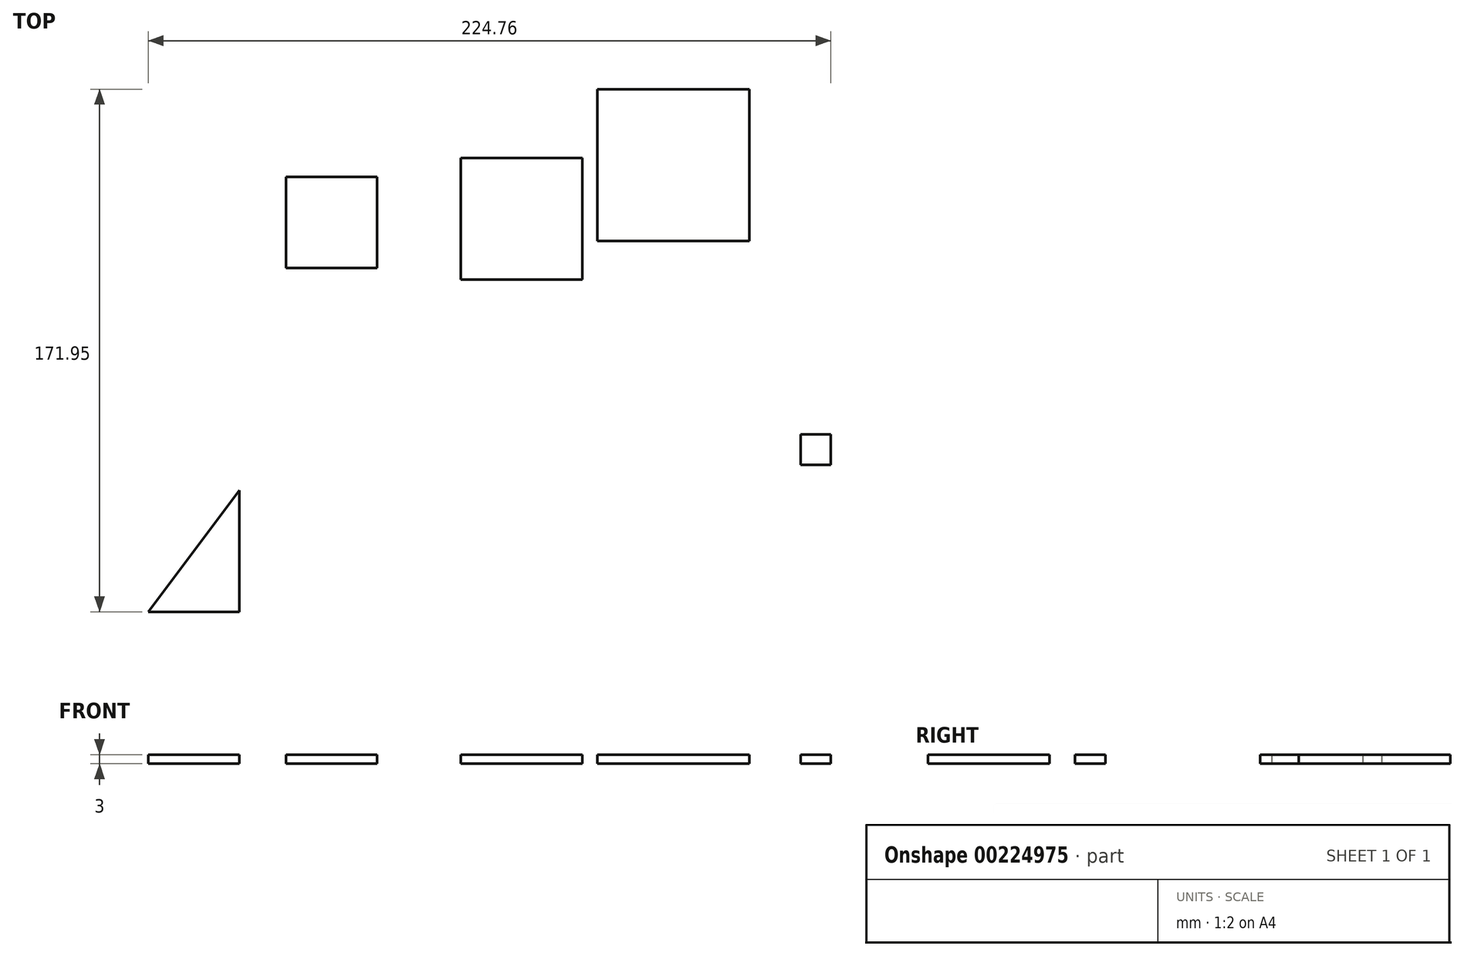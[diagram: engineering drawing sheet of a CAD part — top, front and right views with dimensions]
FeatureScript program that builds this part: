
annotation { "Feature Type Name" : "Feature", "Feature Type Description" : "" }
export const myFeature = defineFeature(function(context is Context, id is Id, definition is map)
    precondition{}
    {
        {
            var Q0;
            Q0=qCreatedBy(makeId("Top.planeOp"),FACE);
            var sketch = newSketch(context, id + "F0", { "sketchPlane" : qUnion([Q0])});
            skLineSegment(sketch, "E0", {"start": v(-120.88, -43.88) * mm, "end": v(-90.88, -43.88) * mm});
            skLineSegment(sketch, "E1", {"start": v(-90.88, -43.88) * mm, "end": v(-90.88, -3.88) * mm});
            skLineSegment(sketch, "E2", {"start": v(-90.88, -3.88) * mm, "end": v(-120.88, -43.88) * mm});
            skLineSegment(sketch, "E3.0.1.1", {"start": v(-121.07, 6.12) * mm, "end": v(-91.07, 6.12) * mm});
            skLineSegment(sketch, "E3.direction1", {"start": v(-120.88, -43.88) * mm, "end": v(-80.9, -42.52) * mm, "construction": true});
            skLineSegment(sketch, "E3.direction2", {"start": v(-120.88, -43.88) * mm, "end": v(-121.07, 6.12) * mm, "construction": true});
            skLineSegment(sketch, "E4.bottom", {"start": v(-75.5, 99.2) * mm, "end": v(-45.5, 99.2) * mm});
            skLineSegment(sketch, "E4.top", {"start": v(-75.5, 69.2) * mm, "end": v(-45.5, 69.2) * mm});
            skLineSegment(sketch, "E4.left", {"start": v(-75.5, 99.2) * mm, "end": v(-75.5, 69.2) * mm});
            skLineSegment(sketch, "E4.right", {"start": v(-45.5, 99.2) * mm, "end": v(-45.5, 69.2) * mm});
            skLineSegment(sketch, "E5.bottom", {"start": v(-17.95, 105.45) * mm, "end": v(22.05, 105.45) * mm});
            skLineSegment(sketch, "E5.top", {"start": v(-17.95, 65.45) * mm, "end": v(22.05, 65.45) * mm});
            skLineSegment(sketch, "E5.left", {"start": v(-17.95, 105.45) * mm, "end": v(-17.95, 65.45) * mm});
            skLineSegment(sketch, "E5.right", {"start": v(22.05, 105.45) * mm, "end": v(22.05, 65.45) * mm});
            skLineSegment(sketch, "E6.bottom", {"start": v(26.98, 128.07) * mm, "end": v(76.98, 128.07) * mm});
            skLineSegment(sketch, "E6.top", {"start": v(26.98, 78.07) * mm, "end": v(76.98, 78.07) * mm});
            skLineSegment(sketch, "E6.left", {"start": v(26.98, 128.07) * mm, "end": v(26.98, 78.07) * mm});
            skLineSegment(sketch, "E6.right", {"start": v(76.98, 128.07) * mm, "end": v(76.98, 78.07) * mm});
            skLineSegment(sketch, "E7.bottom", {"start": v(93.88, 4.48) * mm, "end": v(103.88, 4.48) * mm});
            skLineSegment(sketch, "E7.left", {"start": v(93.88, 4.48) * mm, "end": v(93.88, 14.48) * mm});
            skLineSegment(sketch, "E7.right", {"start": v(103.88, 4.48) * mm, "end": v(103.88, 14.48) * mm});
            skLineSegment(sketch, "E8", {"start": v(103.88, 14.48) * mm, "end": v(93.88, 14.48) * mm});
            skSolve(sketch);
        }
        {
            var Q0;
            Q0 = qSketchRegion(id + "F0", true);
            extrude(context, id + "F1", {"entities" : qUnion([Q0]), "depth" : 3 * mm});
        }
    });
